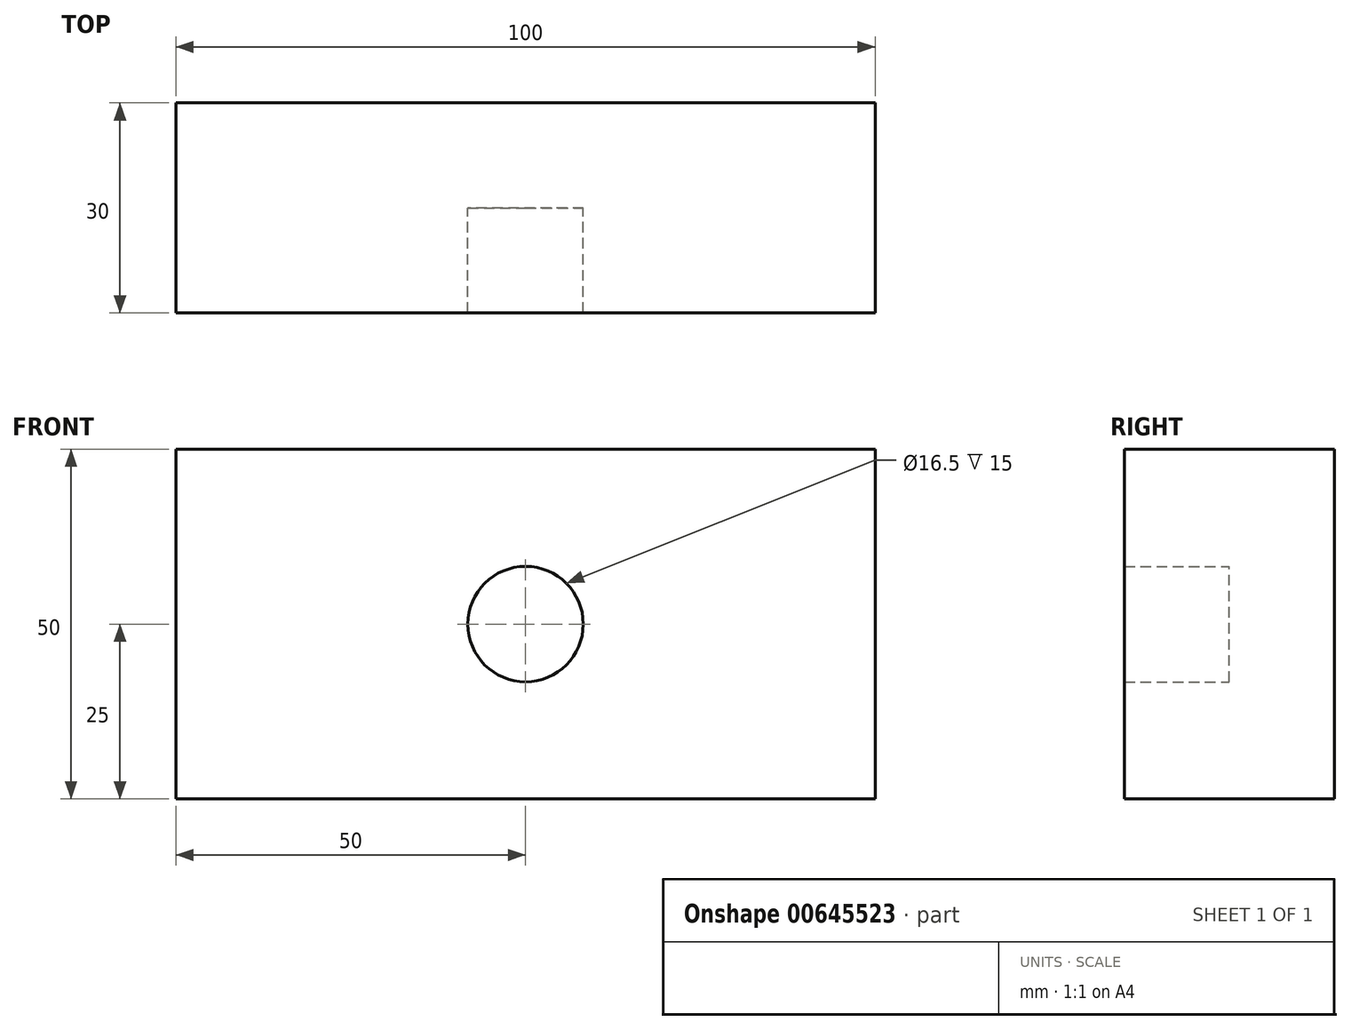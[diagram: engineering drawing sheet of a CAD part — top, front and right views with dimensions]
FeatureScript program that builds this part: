
annotation { "Feature Type Name" : "Feature", "Feature Type Description" : "" }
export const myFeature = defineFeature(function(context is Context, id is Id, definition is map)
    precondition{}
    {
        {
            var Q0;
            Q0=qCreatedBy(makeId("Front.planeOp"),FACE);
            var sketch = newSketch(context, id + "F0", { "sketchPlane" : qUnion([Q0])});
            skLineSegment(sketch, "E0.bottom", {"start": v(-50, 25) * mm, "end": v(50, 25) * mm});
            skLineSegment(sketch, "E0.top", {"start": v(-50, -25) * mm, "end": v(50, -25) * mm});
            skLineSegment(sketch, "E0.left", {"start": v(-50, 25) * mm, "end": v(-50, -25) * mm});
            skLineSegment(sketch, "E0.right", {"start": v(50, 25) * mm, "end": v(50, -25) * mm});
            skPoint(sketch, "E0.middle", {"position": v(0, 0) * mm});
            skSolve(sketch);
        }
        {
            var Q0;
            Q0 = qSketchRegion(id + "F0", true);
            extrude(context, id + "F1", {"entities" : qUnion([Q0]), "endBound" : BoundingType.SYMMETRIC, "depth" : 30 * mm, "offsetDistance" : 25.4 * mm});
        }
        {
            var Q0;
            Q0=qCreatedBy(makeId("Front.planeOp"),FACE);
            var sketch = newSketch(context, id + "F2", { "sketchPlane" : qUnion([Q0])});
            skCircle(sketch, "E1", {"center": v(0, 0) * mm, "radius": 8.25 * mm});
            skSolve(sketch);
        }
        {
            var Q0;
            Q0 = qSketchRegion(id + "F2", true);
            var Q1;
            Q1=makeQuery(id+"F1.opExtrude","CAP_FACE",FACE,{"disambiguationData":[OSD([sQuery(id+"F0.wireOp",EDGE,"E0.bottom"),sQuery(id+"F0.wireOp",EDGE,"E0.top"),sQuery(id+"F0.wireOp",EDGE,"E0.left"),sQuery(id+"F0.wireOp",EDGE,"E0.right")])],"isStart":false});
            extrude(context, id + "F3", {"entities" : qUnion([Q0, Q1]), "operationType" : NewBodyOperationType.REMOVE, "depth" : 20 * mm, "offsetDistance" : 20 * mm});
        }
    });
